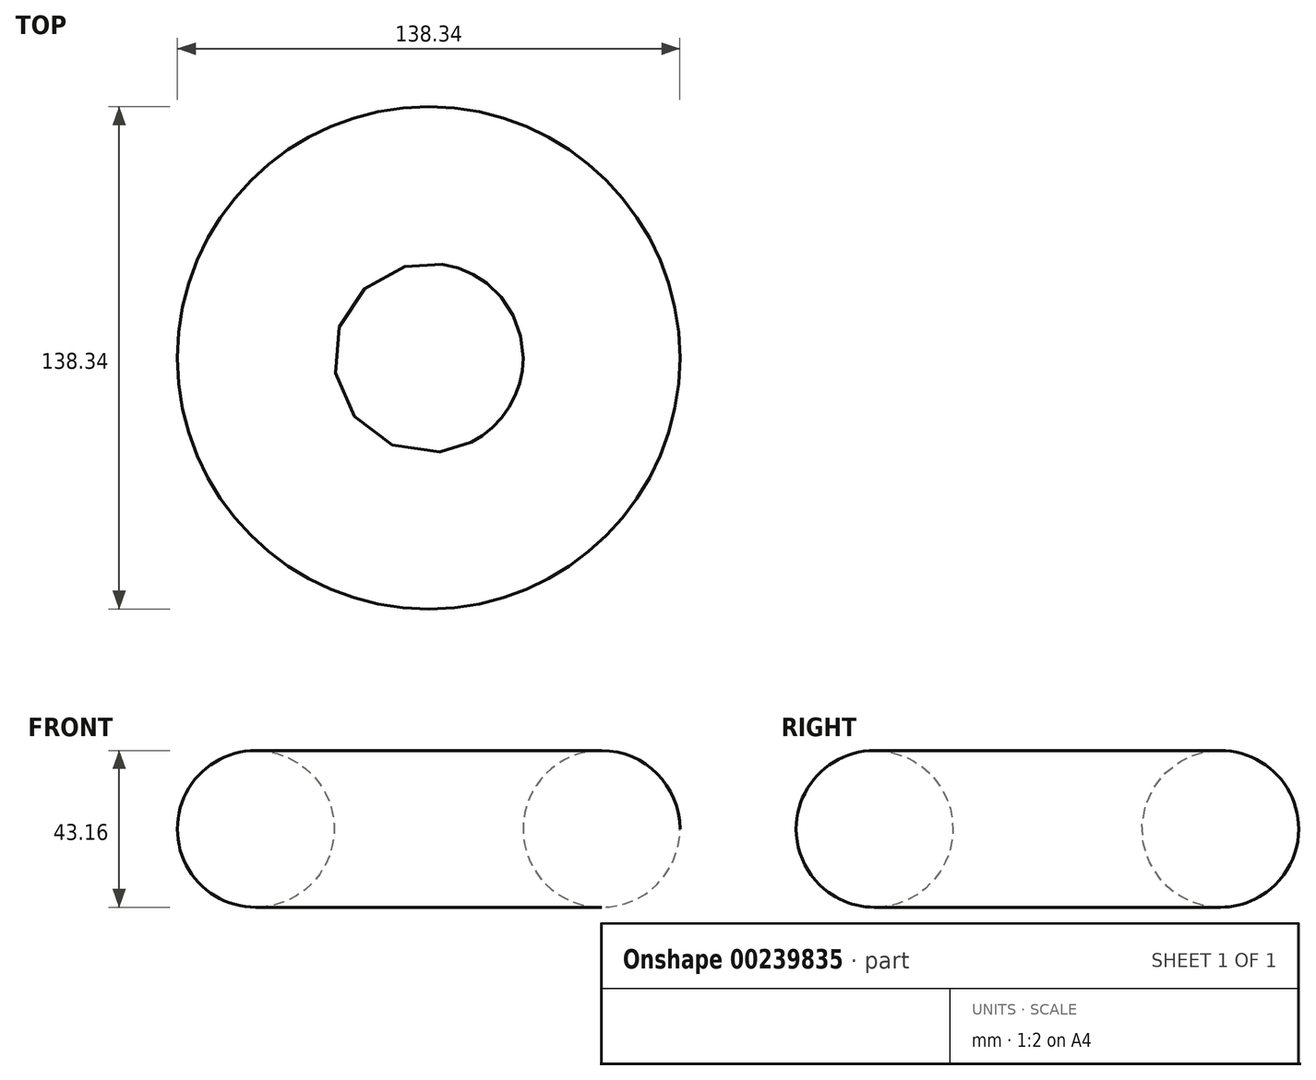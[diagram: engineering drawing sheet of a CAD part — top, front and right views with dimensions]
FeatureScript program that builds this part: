
annotation { "Feature Type Name" : "Feature", "Feature Type Description" : "" }
export const myFeature = defineFeature(function(context is Context, id is Id, definition is map)
    precondition{}
    {
        {
            var Q0;
            Q0=qCreatedBy(makeId("Front.planeOp"),FACE);
            var sketch = newSketch(context, id + "F0", { "sketchPlane" : qUnion([Q0])});
            skCircle(sketch, "E0", {"center": v(-47.6, 44.8) * mm, "radius": 21.58 * mm});
            skSolve(sketch);
        }
        {
            var Q0;
            Q0=qCreatedBy(makeId("Front.planeOp"),FACE);
            var sketch = newSketch(context, id + "F1", { "sketchPlane" : qUnion([Q0])});
            skLineSegment(sketch, "E1", {"start": v(0, 0) * mm, "end": v(0, 71.27) * mm, "construction": true});
            skSolve(sketch);
        }
        {
            var Q0;
            Q0=sQuery(id+"F0.wireOp",EDGE,"E0");
            var Q1;
            Q1=sQuery(id+"F1.wireOp",EDGE,"E1");
            revolve(context, id + "F2", {"bodyType" : ToolBodyType.SURFACE, "surfaceEntities" : qUnion([Q0]), "axis" : qUnion([Q1]), "revolveType" : RevolveType.FULL});
        }
    });
